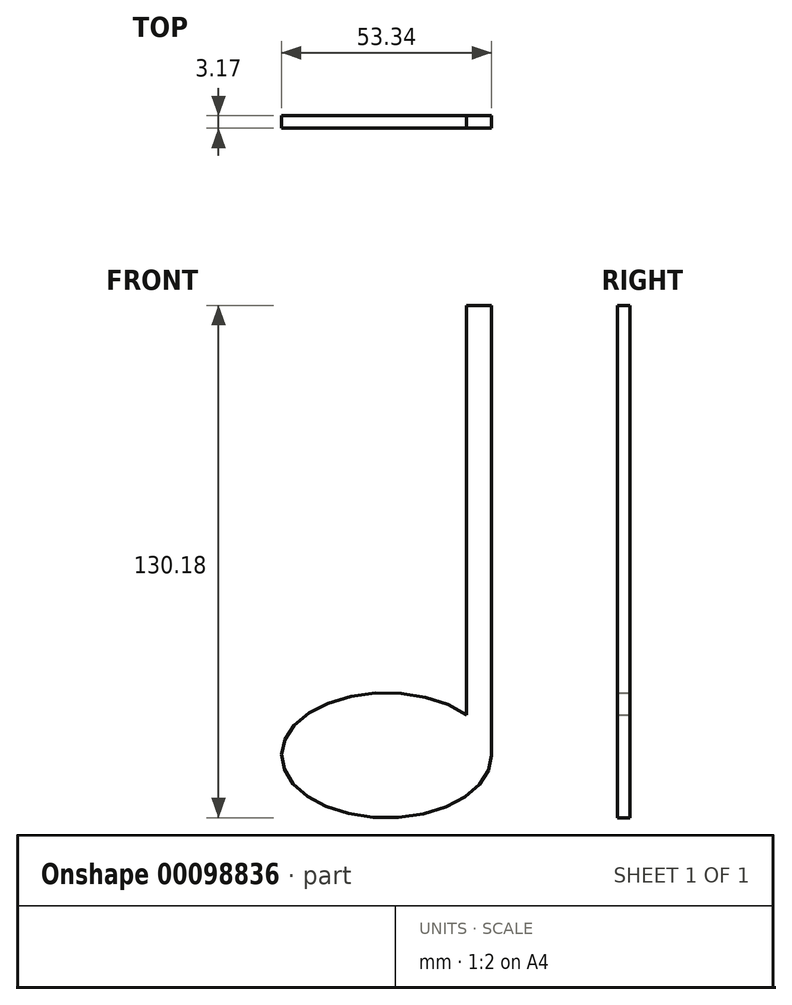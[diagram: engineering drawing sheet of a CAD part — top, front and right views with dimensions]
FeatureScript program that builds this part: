
annotation { "Feature Type Name" : "Feature", "Feature Type Description" : "" }
export const myFeature = defineFeature(function(context is Context, id is Id, definition is map)
    precondition{}
    {
        {
            var Q0;
            Q0=qCreatedBy(makeId("Front.planeOp"),FACE);
            var sketch = newSketch(context, id + "F0", { "sketchPlane" : qUnion([Q0])});
            skEllipticalArc(sketch, "E0", {});
            skLineSegment(sketch, "E1", {"start": v(26.67, 0) * mm, "end": v(26.67, 114.3) * mm});
            skPoint(sketch, "E1.endSnap0", {"position": v(26.67, 0) * mm});
            skLineSegment(sketch, "E2", {"start": v(26.67, 114.3) * mm, "end": v(20.32, 114.3) * mm});
            skLineSegment(sketch, "E3", {"start": v(20.32, 114.3) * mm, "end": v(20.32, 10.28) * mm});
            const initialGuessF0  = {"E0": [0, 0, 1, 0, 0.02667, 0.015875, 0.7045474184528451, 0]};
            skSetInitialGuess(sketch, initialGuessF0);
            skSolve(sketch);
        }
        {
            var Q0;
            Q0 = qSketchRegion(id + "F0", true);
            extrude(context, id + "F1", {"entities" : qUnion([Q0]), "depth" : 3.17 * mm});
        }
    });
